# Revit family: Buzzishade Square
name_source: partatom
category: Lighting Fixtures
revit_build: Autodesk Revit 2018 (Build: 20190510_1515(x64)
units: mm (PartAtom-declared; Revit-internal decimal feet)

## family parameters
Always vertical = Yes
Cut with Voids When Loaded = No
Host = Ceiling
Light Source = Yes
OmniClass Number = 23.80.70.11
OmniClass Title = Luminaries for Internal Lighting
Part Type = Normal
Room Calculation Point = No
Round Connector Dimension = Use Diameter
Shared = No

## types (4) — shared parameters
Color Filter = 16777215
Dimming Lamp Color Temperature Shift = <None>
Light Source Symbol Size = 2' - 0"

## per-type parameters (varying)
| type | Beam Mount | JB Type | Medium Mount | Shade Type |
| Square Beam- Globe | Yes | Junction Box : Beam JB | No | Square Beam Shade : Globe |
| Square Beam- Spot | Yes | Junction Box : Beam JB | No | Square Beam Shade : Spot |
| Square Medium- Globe | No | Junction Box : Medium JB | Yes | Square Medium : Globe |
| Square Medium- Spot | No | Junction Box : Medium JB | Yes | Square Medium : Spot |

## geometry (parser evidence)
native form markers: Sweep x13
no freeform markers — native parametric forms only
